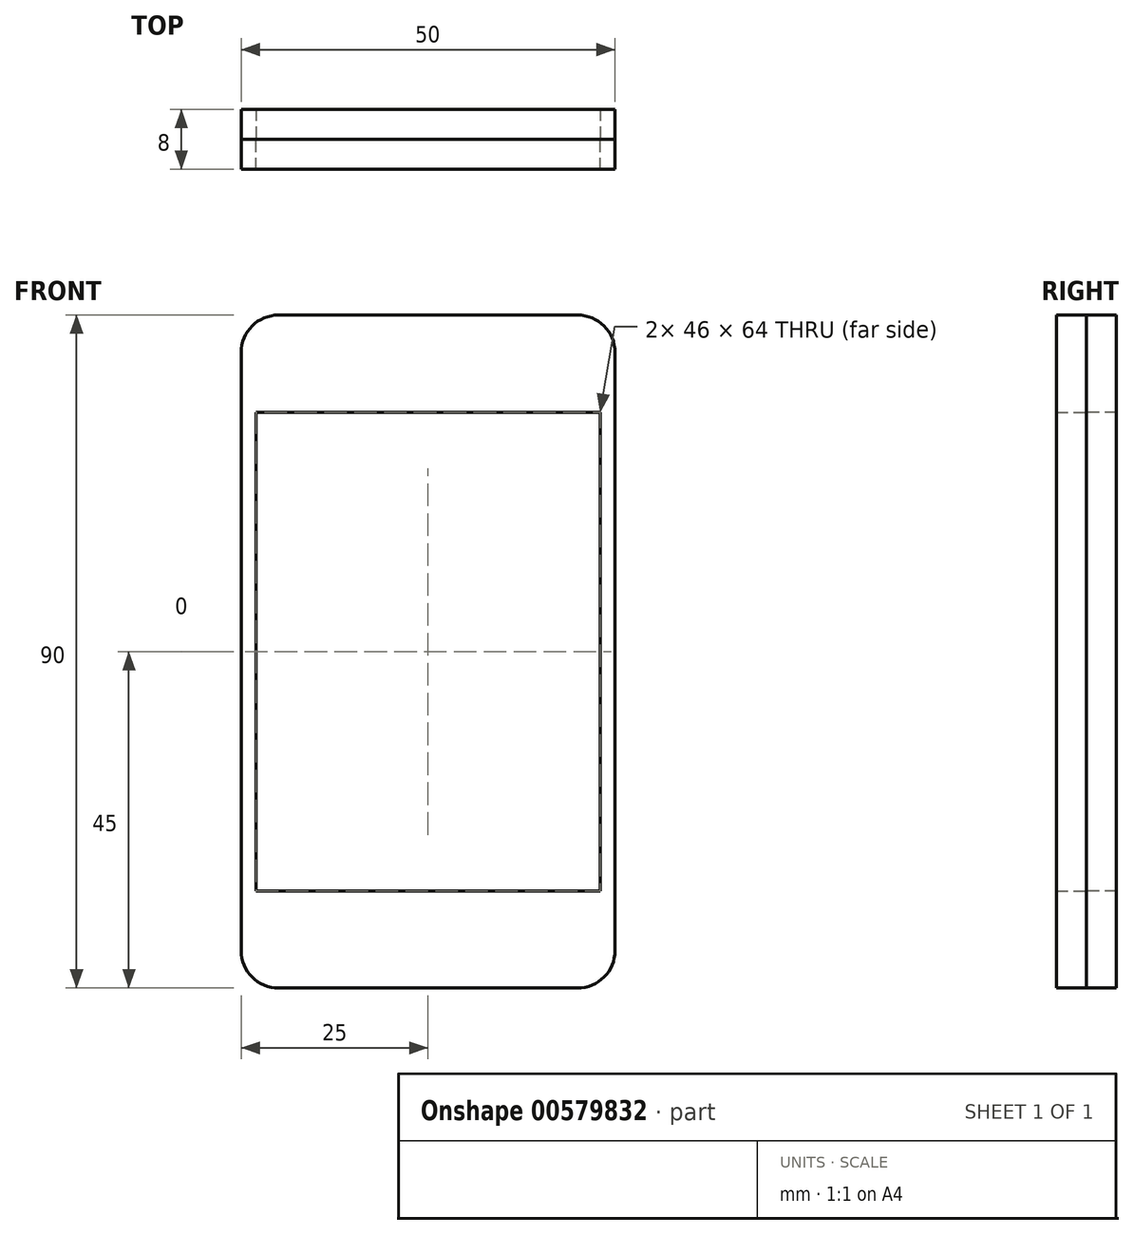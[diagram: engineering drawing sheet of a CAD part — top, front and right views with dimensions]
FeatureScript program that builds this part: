
annotation { "Feature Type Name" : "Feature", "Feature Type Description" : "" }
export const myFeature = defineFeature(function(context is Context, id is Id, definition is map)
    precondition{}
    {
        {
            var Q0;
            Q0=qCreatedBy(makeId("Front.planeOp"),FACE);
            var sketch = newSketch(context, id + "F0", { "sketchPlane" : qUnion([Q0])});
            skLineSegment(sketch, "E0.bottom", {"start": v(-20, 0) * mm, "end": v(20, 0) * mm});
            skLineSegment(sketch, "E0.top", {"start": v(-20, 90) * mm, "end": v(20, 90) * mm});
            skLineSegment(sketch, "E0.left", {"start": v(-25, 5) * mm, "end": v(-25, 85) * mm});
            skLineSegment(sketch, "E0.right", {"start": v(25, 5) * mm, "end": v(25, 85) * mm});
            skPoint(sketch, "E1.visualSharp", {"position": v(-25, 90) * mm});
            skArc(sketch, "E1.filletArc", {"start": v(-20, 90) * mm, "mid": v(-23.54, 88.54) * mm, "end": v(-25, 85) * mm});
            skPoint(sketch, "E2.visualSharp", {"position": v(25, 90) * mm});
            skArc(sketch, "E2.filletArc", {"start": v(25, 85) * mm, "mid": v(23.54, 88.54) * mm, "end": v(20, 90) * mm});
            skPoint(sketch, "E3.visualSharp", {"position": v(25, 0) * mm});
            skArc(sketch, "E3.filletArc", {"start": v(20, 0) * mm, "mid": v(23.54, 1.46) * mm, "end": v(25, 5) * mm});
            skPoint(sketch, "E4.visualSharp", {"position": v(-25, 0) * mm});
            skArc(sketch, "E4.filletArc", {"start": v(-25, 5) * mm, "mid": v(-23.54, 1.46) * mm, "end": v(-20, 0) * mm});
            skPoint(sketch, "E5", {"position": v(0, 0) * mm});
            skLineSegment(sketch, "E6.bottom", {"start": v(-23, 77) * mm, "end": v(23, 77) * mm});
            skLineSegment(sketch, "E6.top", {"start": v(-23, 13) * mm, "end": v(23, 13) * mm});
            skLineSegment(sketch, "E6.left", {"start": v(-23, 77) * mm, "end": v(-23, 13) * mm});
            skLineSegment(sketch, "E6.right", {"start": v(23, 77) * mm, "end": v(23, 13) * mm});
            skSolve(sketch);
        }
        {
            var Q0;
            Q0=makeQuery(id+"F0.imprint","IMPRINT",FACE,{"disambiguationData":[TD([[makeQuery(id+"F0.imprint","IMPRINT",EDGE,{"derivedFrom":sQuery(id+"F0.wireOp",EDGE,"E0.bottom")}),1.0]])]});
            extrude(context, id + "F1", {"entities" : qUnion([Q0]), "depth" : 4 * mm, "offsetDistance" : 25 * mm});
        }
        {
            var Q0;
            Q0=makeQuery(id+"F0.imprint","IMPRINT",FACE,{"disambiguationData":[TD([[makeQuery(id+"F0.imprint","IMPRINT",EDGE,{"derivedFrom":sQuery(id+"F0.wireOp",EDGE,"E0.bottom")}),1.0]])]});
            extrude(context, id + "F2", {"entities" : qUnion([Q0]), "oppositeDirection" : true, "depth" : 4 * mm, "offsetDistance" : 25 * mm});
        }
    });
